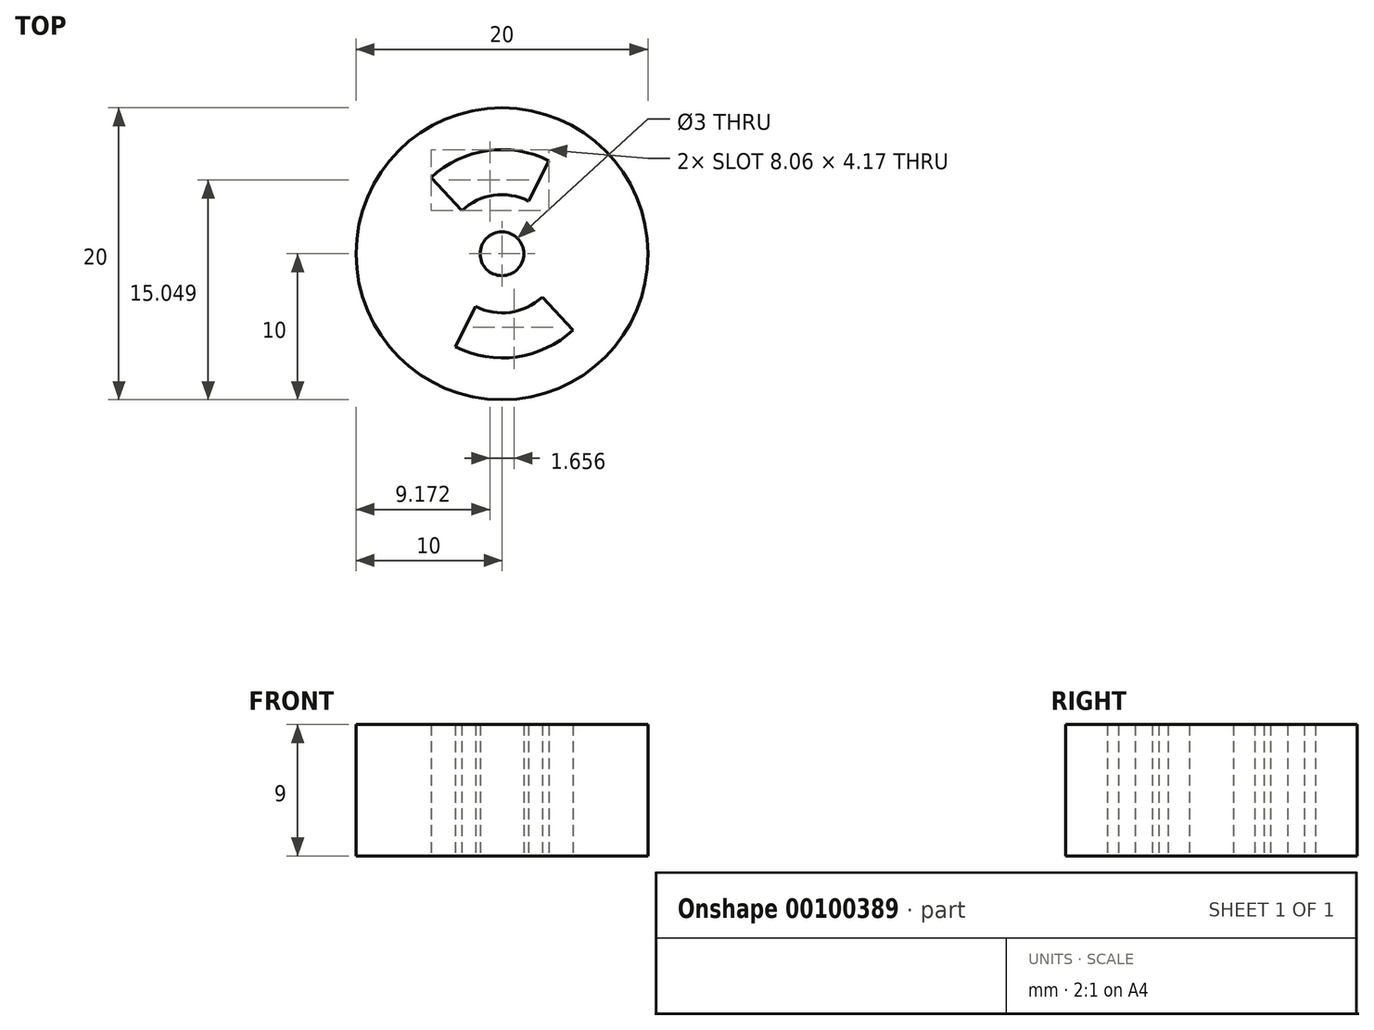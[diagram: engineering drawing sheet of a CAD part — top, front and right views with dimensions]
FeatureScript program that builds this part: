
annotation { "Feature Type Name" : "Feature", "Feature Type Description" : "" }
export const myFeature = defineFeature(function(context is Context, id is Id, definition is map)
    precondition{}
    {
        {
            var Q0;
            Q0=qCreatedBy(makeId("Top.planeOp"),FACE);
            var sketch = newSketch(context, id + "F0", { "sketchPlane" : qUnion([Q0])});
            skCircle(sketch, "E0", {"center": v(0, 0) * mm, "radius": 10 * mm});
            skCircle(sketch, "E1", {"center": v(0, 0) * mm, "radius": 1.5 * mm});
            skArc(sketch, "E2", {"start": v(-1.82, -3.62) * mm, "mid": v(0.57, -4) * mm, "end": v(2.76, -2.96) * mm});
            skArc(sketch, "E3", {"start": v(3.2, 6.38) * mm, "mid": v(-1, 7.06) * mm, "end": v(-4.86, 5.22) * mm});
            skLineSegment(sketch, "E4", {"start": v(-4.86, 5.22) * mm, "end": v(-2.76, 2.96) * mm});
            skLineSegment(sketch, "E5", {"start": v(2.76, -2.96) * mm, "end": v(4.86, -5.22) * mm});
            skLineSegment(sketch, "E6", {"start": v(-3.2, -6.38) * mm, "end": v(-1.82, -3.62) * mm});
            skLineSegment(sketch, "E7", {"start": v(1.82, 3.62) * mm, "end": v(3.2, 6.38) * mm});
            skLineSegment(sketch, "E8.trimOffspring", {"start": v(-2.76, 2.96) * mm, "end": v(-4.86, 5.22) * mm});
            skArc(sketch, "E9.trimOffspring", {"start": v(1.82, 3.62) * mm, "mid": v(-0.57, 4) * mm, "end": v(-2.76, 2.96) * mm});
            skArc(sketch, "E10.trimOffspring", {"start": v(-3.2, -6.38) * mm, "mid": v(1, -7.06) * mm, "end": v(4.86, -5.22) * mm});
            skSolve(sketch);
        }
        {
            var Q0;
            Q0=makeQuery(id+"F0.imprint","IMPRINT",FACE,{"disambiguationData":[TD([[makeQuery(id+"F0.imprint","IMPRINT",EDGE,{"derivedFrom":sQuery(id+"F0.wireOp",EDGE,"E0")}),1.0]])]});
            var Q1;
            {var subQ5=sQuery(id+"F0.wireOp",EDGE,"BsZpd01B-x193-d97P-swnW-OA9iiEq2pzff.top");Q1=makeQuery(id+"F0.imprint","IMPRINT",FACE,{"disambiguationData":[TD([[makeQuery(id+"F0.imprint","IMPRINT",EDGE,{"derivedFrom":subQ5}),-1.0]])]});}
            extrude(context, id + "F1", {"entities" : qUnion([Q0, Q1]), "depth" : 9 * mm});
        }
    });
